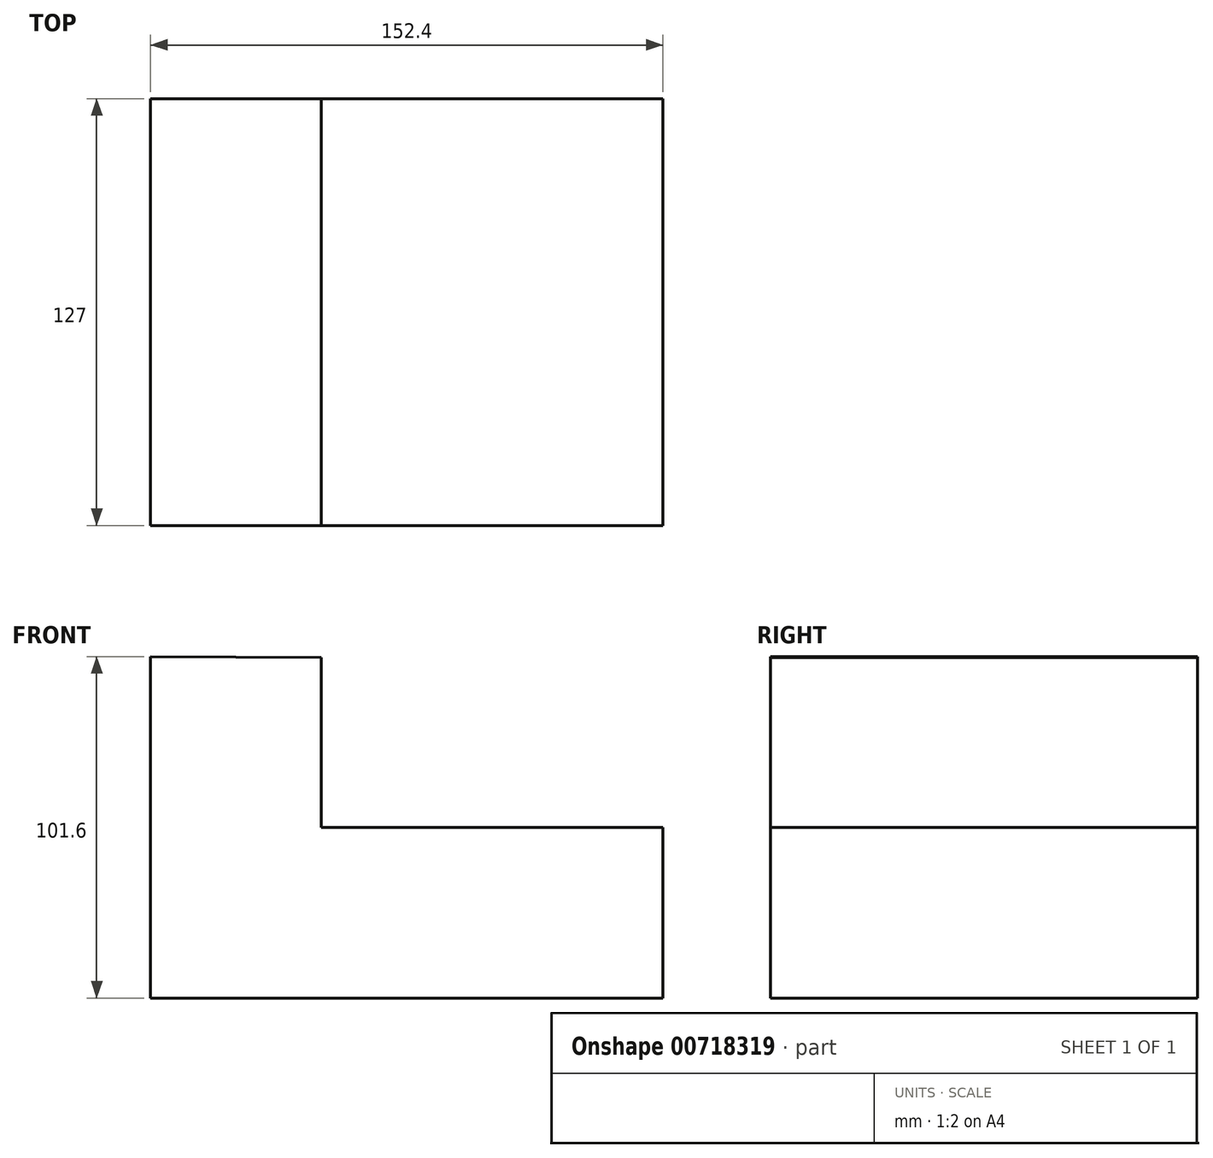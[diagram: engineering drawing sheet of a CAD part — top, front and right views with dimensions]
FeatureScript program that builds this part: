
annotation { "Feature Type Name" : "Feature", "Feature Type Description" : "" }
export const myFeature = defineFeature(function(context is Context, id is Id, definition is map)
    precondition{}
    {
        {
            var Q0;
            Q0=qCreatedBy(makeId("Front.planeOp"),FACE);
            var sketch = newSketch(context, id + "F0", { "sketchPlane" : qUnion([Q0])});
            skLineSegment(sketch, "E0", {"start": v(-73.67, -20.3) * mm, "end": v(78.73, -20.3) * mm});
            skLineSegment(sketch, "E1", {"start": v(-73.67, -20.3) * mm, "end": v(-73.67, 81.3) * mm});
            skLineSegment(sketch, "E2", {"start": v(-73.67, -20.3) * mm, "end": v(-22.87, -20.3) * mm});
            skLineSegment(sketch, "E3", {"start": v(78.73, -20.3) * mm, "end": v(78.73, 30.5) * mm});
            skLineSegment(sketch, "E4", {"start": v(78.73, 30.5) * mm, "end": v(-22.87, 30.5) * mm});
            skLineSegment(sketch, "E5", {"start": v(-22.87, 30.5) * mm, "end": v(-22.87, 80.94) * mm});
            skLineSegment(sketch, "E6", {"start": v(-73.67, 81.3) * mm, "end": v(-22.87, 80.94) * mm});
            skSolve(sketch);
        }
        {
            var Q0;
            Q0=makeQuery(id+"F0.imprint","IMPRINT",FACE,{"disambiguationData":[TD([[makeQuery(id+"F0.imprint","IMPRINT",EDGE,{"derivedFrom":sQuery(id+"F0.wireOp",EDGE,"E0")}),1.0]])]});
            extrude(context, id + "F1", {"entities" : qUnion([Q0]), "depth" : 127 * mm, "offsetDistance" : 25.4 * mm});
        }
    });
